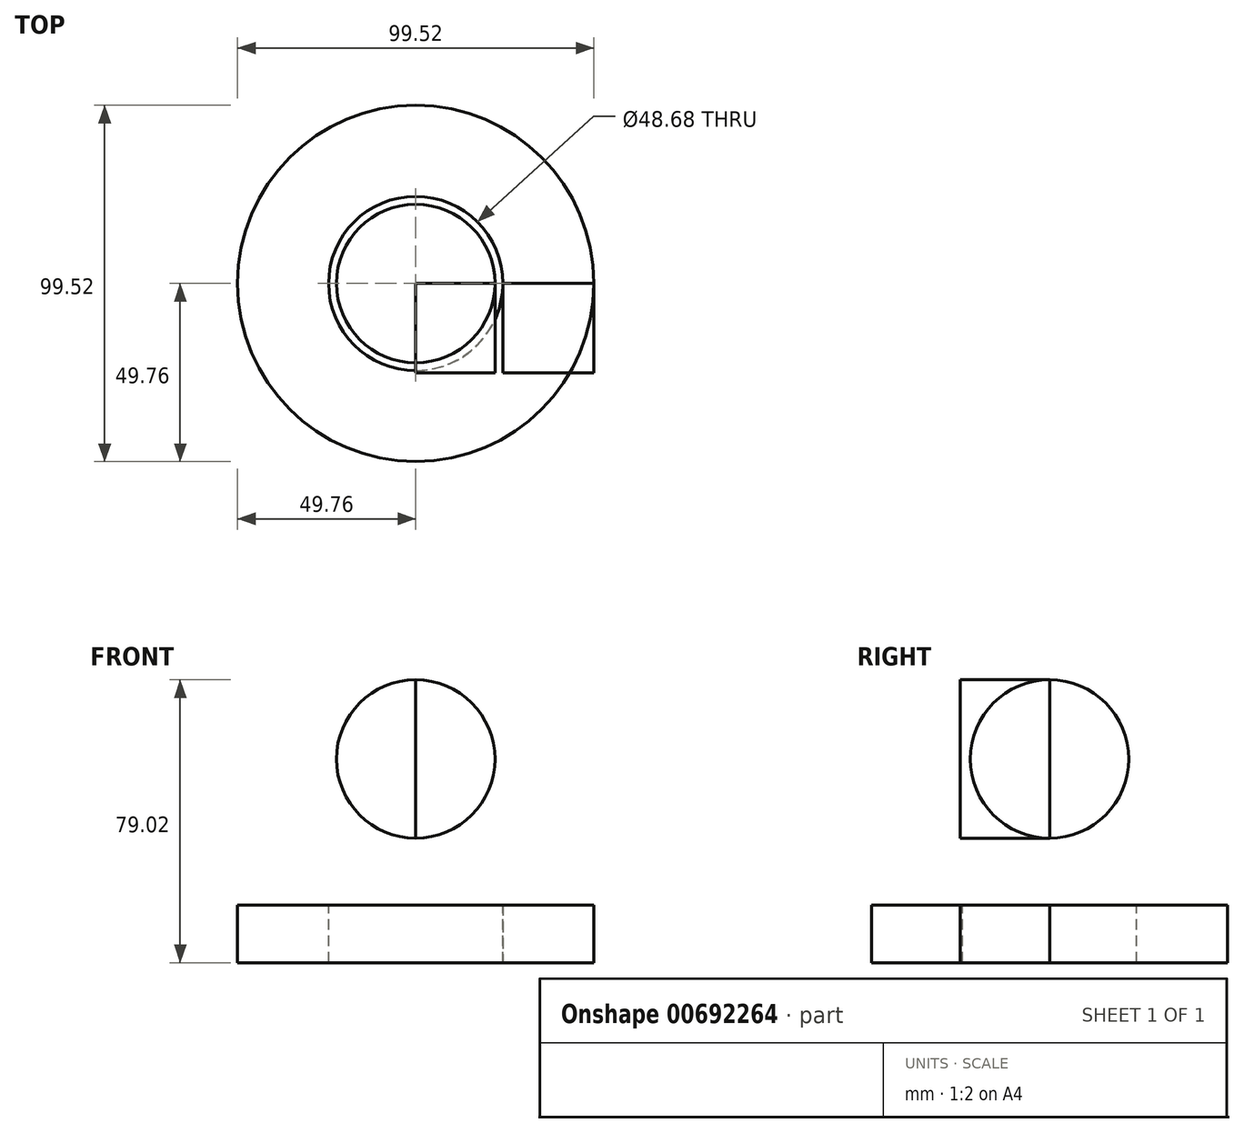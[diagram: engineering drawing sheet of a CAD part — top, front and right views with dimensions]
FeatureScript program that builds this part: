
annotation { "Feature Type Name" : "Feature", "Feature Type Description" : "" }
export const myFeature = defineFeature(function(context is Context, id is Id, definition is map)
    precondition{}
    {
        {
            var Q0;
            Q0=qCreatedBy(makeId("Front.planeOp"),FACE);
            var sketch = newSketch(context, id + "F0", { "sketchPlane" : qUnion([Q0])});
            skArc(sketch, "E0", {"start": v(0, -22.13) * mm, "mid": v(22.13, 0) * mm, "end": v(0, 22.13) * mm});
            skLineSegment(sketch, "E1", {"start": v(0, 30.54) * mm, "end": v(0, -35.19) * mm, "construction": true});
            skLineSegment(sketch, "E2", {"start": v(0, 22.13) * mm, "end": v(0, -22.13) * mm});
            skLineSegment(sketch, "E3.bottom", {"start": v(24.34, -40.77) * mm, "end": v(49.76, -40.77) * mm});
            skLineSegment(sketch, "E3.top", {"start": v(24.34, -56.9) * mm, "end": v(49.76, -56.9) * mm});
            skLineSegment(sketch, "E3.left", {"start": v(24.34, -40.77) * mm, "end": v(24.34, -56.9) * mm});
            skLineSegment(sketch, "E3.right", {"start": v(49.76, -40.77) * mm, "end": v(49.76, -56.9) * mm});
            skSolve(sketch);
        }
        {
            var Q0;
            Q0 = qSketchRegion(id + "F0", true);
            var Q1;
            Q1=sQuery(id+"F0.wireOp",EDGE,"E1");
            revolve(context, id + "F1", {"entities" : qUnion([Q0]), "axis" : qUnion([Q1]), "revolveType" : RevolveType.FULL});
        }
        {
            var Q0;
            Q0 = qSketchRegion(id + "F0", true);
            extrude(context, id + "F2", {"entities" : qUnion([Q0]), "depth" : 25 * mm, "offsetDistance" : 25 * mm});
        }
    });
